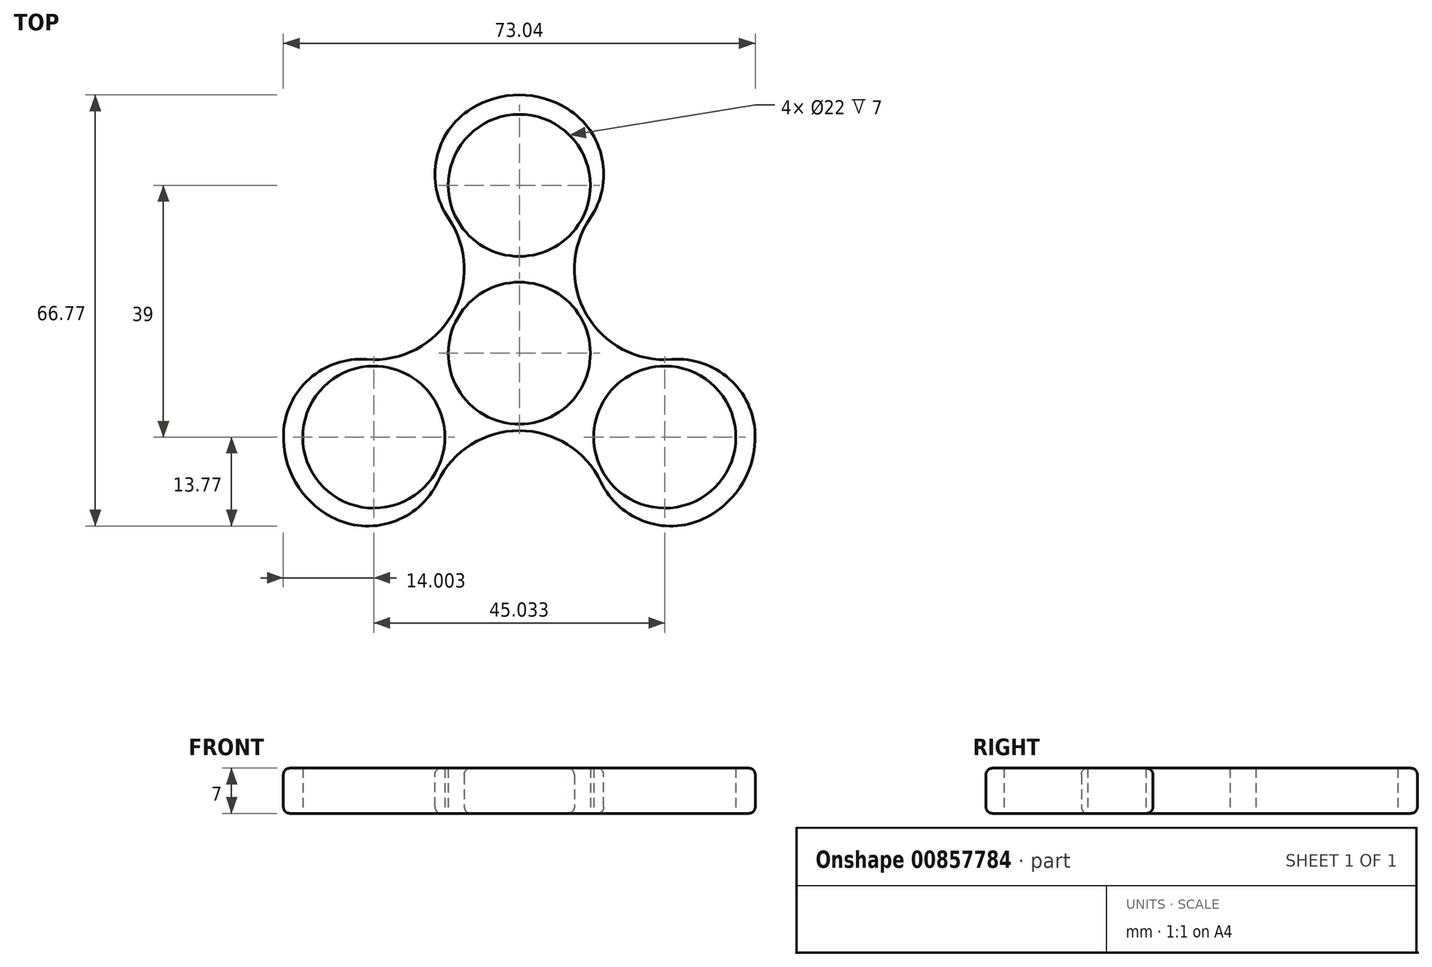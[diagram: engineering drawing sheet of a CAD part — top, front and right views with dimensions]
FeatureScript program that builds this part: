
annotation { "Feature Type Name" : "Feature", "Feature Type Description" : "" }
export const myFeature = defineFeature(function(context is Context, id is Id, definition is map)
    precondition{}
    {
        {
            var Q0;
            Q0=qCreatedBy(makeId("Top.planeOp"),FACE);
            var sketch = newSketch(context, id + "F0", { "sketchPlane" : qUnion([Q0])});
            skArc(sketch, "E0", {"start": v(13.86, 24) * mm, "mid": v(0, 40) * mm, "end": v(-13.86, 24) * mm});
            skCircle(sketch, "E1", {"center": v(0, 26) * mm, "radius": 11 * mm});
            skArc(sketch, "E2.1.0", {"start": v(-27.71, 0) * mm, "mid": v(-10.4, 6) * mm, "end": v(-13.86, 24) * mm});
            skArc(sketch, "E2.2.0", {"start": v(-27.71, 0) * mm, "mid": v(-34.64, -20) * mm, "end": v(-13.86, -24) * mm});
            skArc(sketch, "E2.3.0", {"start": v(13.86, -24) * mm, "mid": v(0, -12) * mm, "end": v(-13.86, -24) * mm});
            skArc(sketch, "E2.5.0", {"start": v(13.86, 24) * mm, "mid": v(10.4, 6) * mm, "end": v(27.71, 0) * mm});
            skPoint(sketch, "E2.center", {"position": v(0, 0) * mm});
            skArc(sketch, "E3.trimOffspring", {"start": v(13.86, -24) * mm, "mid": v(34.64, -20) * mm, "end": v(27.71, 0) * mm});
            skPoint(sketch, "E4.orphan", {"position": v(1.67, -12.99) * mm});
            skPoint(sketch, "E5.orphan", {"position": v(8.85, -16.06) * mm});
            skPoint(sketch, "E6.orphan", {"position": v(-9.48, -15.7) * mm});
            skPoint(sketch, "E7.orphan", {"position": v(-2.96, -12.32) * mm});
            skPoint(sketch, "E8.orphan", {"position": v(-8.85, 16.06) * mm});
            skPoint(sketch, "E9.orphan", {"position": v(-9.19, 8.72) * mm});
            skPoint(sketch, "E10.orphan", {"position": v(12.15, 3.6) * mm});
            skPoint(sketch, "E11.orphan", {"position": v(18.33, -0.36) * mm});
            skCircle(sketch, "E12", {"center": v(-22.52, -13) * mm, "radius": 11 * mm});
            skCircle(sketch, "E13", {"center": v(22.52, -13) * mm, "radius": 11 * mm});
            skCircle(sketch, "E14", {"center": v(0, 0) * mm, "radius": 11 * mm});
            skSolve(sketch);
        }
        {
            var Q0;
            Q0=makeQuery(id+"F0.imprint","IMPRINT",FACE,{"disambiguationData":[TD([[makeQuery(id+"F0.imprint","IMPRINT",EDGE,{"derivedFrom":sQuery(id+"F0.wireOp",EDGE,"E0")}),1.0]])]});
            extrude(context, id + "F1", {"entities" : qUnion([Q0]), "depth" : 7 * mm, "offsetDistance" : 25 * mm});
        }
        {
            var Q0;
            Q0=makeQuery(id+"F1.opExtrude","SWEPT_EDGE",EDGE,{"disambiguationData":[OSD([sQuery(id+"F0.wireOp",EDGE,"E0"),sQuery(id+"F0.wireOp",EDGE,"E2.1.0")])]});
            var Q1;
            Q1=makeQuery(id+"F1.opExtrude","SWEPT_EDGE",EDGE,{"disambiguationData":[OSD([sQuery(id+"F0.wireOp",EDGE,"E2.1.0"),sQuery(id+"F0.wireOp",EDGE,"E2.2.0")])]});
            var Q2;
            Q2=makeQuery(id+"F1.opExtrude","SWEPT_EDGE",EDGE,{"disambiguationData":[OSD([sQuery(id+"F0.wireOp",EDGE,"E2.5.0"),sQuery(id+"F0.wireOp",EDGE,"E3.trimOffspring")])]});
            var Q3;
            Q3=makeQuery(id+"F1.opExtrude","SWEPT_EDGE",EDGE,{"disambiguationData":[OSD([sQuery(id+"F0.wireOp",EDGE,"E2.3.0"),sQuery(id+"F0.wireOp",EDGE,"E3.trimOffspring")])]});
            var Q4;
            Q4=makeQuery(id+"F1.opExtrude","SWEPT_EDGE",EDGE,{"disambiguationData":[OSD([sQuery(id+"F0.wireOp",EDGE,"E0"),sQuery(id+"F0.wireOp",EDGE,"E2.5.0")])]});
            var Q5;
            Q5=makeQuery(id+"F1.opExtrude","SWEPT_EDGE",EDGE,{"disambiguationData":[OSD([sQuery(id+"F0.wireOp",EDGE,"E2.2.0"),sQuery(id+"F0.wireOp",EDGE,"E2.3.0")])]});
            fillet(context, id + "F2", {"entities" : qUnion([Q0, Q1, Q2, Q3, Q4, Q5]), "radius" : 12 * mm, "tangentPropagation" : true, "allowEdgeOverflow" : false});
        }
        {
            var Q0;
            Q0=makeQuery(id+"F1.opExtrude","CAP_EDGE",EDGE,{"disambiguationData":[OSD([sQuery(id+"F0.wireOp",EDGE,"E2.3.0")])],"isStart":true});
            fillet(context, id + "F3", {"entities" : qUnion([Q0]), "radius" : 1 * mm, "tangentPropagation" : true, "allowEdgeOverflow" : false});
        }
        {
            var Q0;
            Q0=makeQuery(id+"F1.opExtrude","CAP_EDGE",EDGE,{"disambiguationData":[OSD([sQuery(id+"F0.wireOp",EDGE,"E2.5.0")])],"isStart":false});
            fillet(context, id + "F4", {"entities" : qUnion([Q0]), "radius" : 1 * mm, "tangentPropagation" : true, "allowEdgeOverflow" : false});
        }
    });
